FCSTD DOCUMENT  (FreeCAD 0.20R0.20)
Label: 006
License: All rights reserved
LicenseURL: http://en.wikipedia.org/wiki/All_rights_reserved
objects: Sketcher::SketchObject×1
note: 1 computed .brp shape members not serialized (recipe doc carries the construction recipe); baked Part::Feature solids carry a one-line shape summary decoded from their .brp

FEATURE [Sketcher::SketchObject] Sketch
  FullyConstrained = true
  sketch-geometry (36):
    g0: LineSegment StartX=80 StartY=80 StartZ=0 EndX=74 EndY=80 EndZ=0
    g1: LineSegment StartX=80 StartY=80 StartZ=0 EndX=80 EndY=74 EndZ=0
    g2: LineSegment StartX=0 StartY=80 StartZ=0 EndX=6 EndY=80 EndZ=0
    g3: LineSegment StartX=80 StartY=0 StartZ=0 EndX=80 EndY=6 EndZ=0
    g4: LineSegment StartX=0 StartY=0 StartZ=0 EndX=0 EndY=6 EndZ=0
    g5: LineSegment StartX=0 StartY=0 StartZ=0 EndX=6 EndY=0 EndZ=0
    g6: LineSegment StartX=80 StartY=0 StartZ=0 EndX=74 EndY=0 EndZ=0
    g7: LineSegment StartX=0 StartY=80 StartZ=0 EndX=0 EndY=74 EndZ=0
    g8: LineSegment StartX=54 StartY=58 StartZ=0 EndX=40 EndY=44 EndZ=0
    g9: LineSegment StartX=26 StartY=22 StartZ=0 EndX=40 EndY=36 EndZ=0
    g10: LineSegment StartX=26 StartY=58 StartZ=0 EndX=40 EndY=44 EndZ=0
    g11: LineSegment StartX=6 StartY=70 StartZ=0 EndX=10 EndY=66 EndZ=0
    g12: LineSegment StartX=40 StartY=36 StartZ=0 EndX=54 EndY=22 EndZ=0
    g13: LineSegment StartX=44 StartY=40 StartZ=0 EndX=54 EndY=30 EndZ=0
    g14: LineSegment StartX=36 StartY=40 StartZ=0 EndX=26 EndY=30 EndZ=0
    g15: LineSegment StartX=44 StartY=40 StartZ=0 EndX=54 EndY=50 EndZ=0
    g16: LineSegment StartX=74 StartY=10 StartZ=0 EndX=74 EndY=70 EndZ=0
    g17: LineSegment StartX=26 StartY=6 StartZ=0 EndX=54 EndY=6 EndZ=0
    g18: LineSegment StartX=6 StartY=70 StartZ=0 EndX=6 EndY=10 EndZ=0
    g19: LineSegment StartX=6 StartY=80 StartZ=0 EndX=74 EndY=80 EndZ=0
    g20: LineSegment StartX=80 StartY=74 StartZ=0 EndX=80 EndY=6 EndZ=0
    g21: LineSegment StartX=74 StartY=0 StartZ=0 EndX=6 EndY=0 EndZ=0
    g22: LineSegment StartX=0 StartY=6 StartZ=0 EndX=0 EndY=74 EndZ=0
    g23: LineSegment StartX=10 StartY=66 StartZ=0 EndX=10 EndY=14 EndZ=0
    g24: LineSegment StartX=70 StartY=66 StartZ=0 EndX=70 EndY=14 EndZ=0
    g25: LineSegment StartX=26 StartY=74 StartZ=0 EndX=26 EndY=58 EndZ=0
    g26: LineSegment StartX=54 StartY=74 StartZ=0 EndX=54 EndY=58 EndZ=0
    g27: LineSegment StartX=26 StartY=74 StartZ=0 EndX=54 EndY=74 EndZ=0
    g28: LineSegment StartX=26 StartY=50 StartZ=0 EndX=36 EndY=40 EndZ=0
    g29: LineSegment StartX=70 StartY=66 StartZ=0 EndX=74 EndY=70 EndZ=0
    g30: LineSegment StartX=70 StartY=14 StartZ=0 EndX=74 EndY=10 EndZ=0
    g31: LineSegment StartX=10 StartY=14 StartZ=0 EndX=6 EndY=10 EndZ=0
    g32: LineSegment StartX=54 StartY=22 StartZ=0 EndX=54 EndY=6 EndZ=0
    g33: LineSegment StartX=26 StartY=22 StartZ=0 EndX=26 EndY=6 EndZ=0
    g34: LineSegment StartX=54 StartY=50 StartZ=0 EndX=54 EndY=30 EndZ=0
    g35: LineSegment StartX=26 StartY=50 StartZ=0 EndX=26 EndY=30 EndZ=0
  constraints (83):
    c: Horizontal(g0)
    c: Distance(g0) = 6
    c: Block(g0)
    c: Coincident(g1,g0)
    c: Vertical(g1)
    c: Horizontal(g2)
    c: Vertical(g3)
    c: Distance(g1) = 6
    c: Distance(g2) = 6
    c: Distance(g3) = 6
    c: Block(g2)
    c: Block(g3)
    c: Coincident(g4,g-1)
    c: Vertical(g4)
    c: Coincident(g5,g4)
    c: Horizontal(g5)
    c: Coincident(g6,g3)
    c: Horizontal(g6)
    c: Coincident(g7,g2)
    c: Vertical(g7)
    c: Distance(g7) = 6
    c: Distance(g4) = 6
    c: Distance(g5) = 6
    c: Distance(g6) = 6
    c: Coincident(g8,g10)
    c: Coincident(g14,g28)
    c: Coincident(g9,g12)
    c: Coincident(g15,g13)
    c: Block(g15)
    c: Block(g8)
    c: Block(g14)
    c: Block(g12)
    c: Block(g13)
    c: Block(g9)
    c: Block(g11)
    c: Block(g10)
    c: Block(g16)
    c: Block(g17)
    c: Block(g18)
    c: Coincident(g29,g16)
    c: Coincident(g30,g16)
    c: Coincident(g31,g18)
    c: Coincident(g11,g18)
    c: Coincident(g19,g2)
    c: Coincident(g19,g0)
    c: Horizontal(g19)
    c: Coincident(g20,g1)
    c: Coincident(g20,g3)
    c: Vertical(g20)
    c: Coincident(g21,g6)
    c: Coincident(g21,g5)
    c: Horizontal(g21)
    c: Coincident(g22,g4)
    c: Coincident(g22,g7)
    c: Vertical(g22)
    c: Vertical(g23)
    c: Vertical(g24)
    c: Vertical(g25)
    c: Vertical(g26)
    c: Horizontal(g27)
    c: Block(g27)
    c: Block(g26)
    c: Block(g25)
    c: Block(g23)
    c: Block(g24)
    c: Block(g29)
    c: Block(g31)
    c: Block(g30)
    c: Block(g28)
    c: Coincident(g23,g11)
    c: Coincident(g24,g29)
    c: Coincident(g24,g30)
    c: Coincident(g17,g32)
    c: Coincident(g23,g31)
    c: Coincident(g17,g33)
    c: Coincident(g34,g13)
    c: Coincident(g32,g12)
    c: Coincident(g35,g14)
    c: Coincident(g33,g9)
    c: Coincident(g26,g8)
    c: Coincident(g34,g15)
    c: Coincident(g25,g10)
    c: Coincident(g35,g28)
